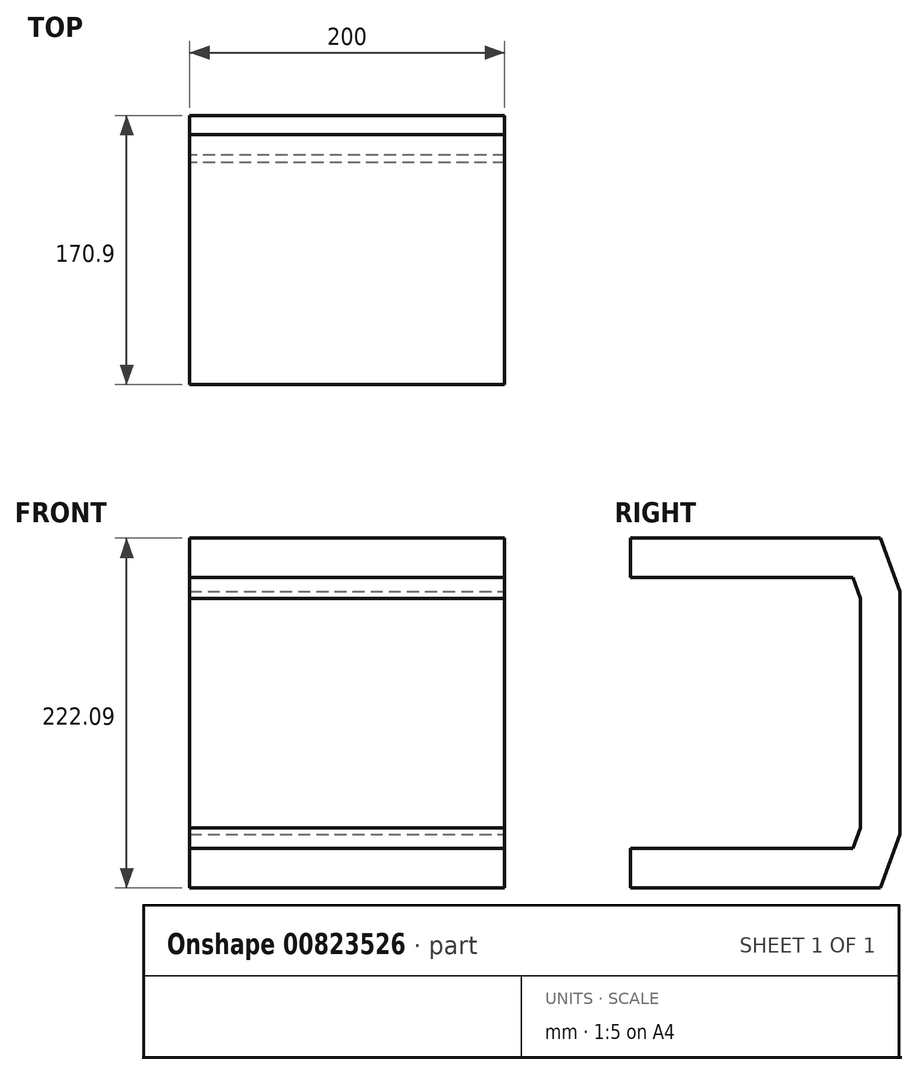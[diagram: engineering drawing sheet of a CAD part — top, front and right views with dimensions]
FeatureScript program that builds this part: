
annotation { "Feature Type Name" : "Feature", "Feature Type Description" : "" }
export const myFeature = defineFeature(function(context is Context, id is Id, definition is map)
    precondition{}
    {
        {
            var Q0;
            Q0=qCreatedBy(makeId("Front.planeOp"),FACE);
            var sketch = newSketch(context, id + "F0", { "sketchPlane" : qUnion([Q0])});
            skLineSegment(sketch, "E0.bottom", {"start": v(100, -12.5) * mm, "end": v(-100, -12.5) * mm});
            skLineSegment(sketch, "E0.top", {"start": v(100, 12.5) * mm, "end": v(-100, 12.5) * mm});
            skLineSegment(sketch, "E0.left", {"start": v(100, -12.5) * mm, "end": v(100, 12.5) * mm});
            skLineSegment(sketch, "E0.right", {"start": v(-100, -12.5) * mm, "end": v(-100, 12.5) * mm});
            skPoint(sketch, "E0.middle", {"position": v(0, 0) * mm});
            skSolve(sketch);
        }
        {
            var Q0;
            Q0=qCreatedBy(makeId("Right.planeOp"),FACE);
            var sketch = newSketch(context, id + "F1", { "sketchPlane" : qUnion([Q0])});
            skLineSegment(sketch, "E1", {"start": v(0, 0) * mm, "end": v(150, 0) * mm});
            skLineSegment(sketch, "E2", {"start": v(150, 0) * mm, "end": v(158.4, 23.55) * mm});
            skLineSegment(sketch, "E3", {"start": v(158.4, 23.55) * mm, "end": v(158.4, 173.55) * mm});
            skLineSegment(sketch, "E4", {"start": v(158.4, 173.55) * mm, "end": v(150, 197.1) * mm});
            skLineSegment(sketch, "E5", {"start": v(150, 197.1) * mm, "end": v(0, 197.1) * mm});
            skSolve(sketch);
        }
        {
            var Q0;
            Q0 = qSketchRegion(id + "F0", true);
            var Q1;
            Q1=sQuery(id+"F1.wireOp",EDGE,"E2");
            var Q2;
            Q2=sQuery(id+"F1.wireOp",EDGE,"E1");
            var Q3;
            Q3=sQuery(id+"F1.wireOp",EDGE,"E3");
            var Q4;
            Q4=sQuery(id+"F1.wireOp",EDGE,"E4");
            var Q5;
            Q5=sQuery(id+"F1.wireOp",EDGE,"E5");
            sweep(context, id + "F2", {"profiles" : qUnion([Q0]), "path" : qUnion([Q1, Q2, Q3, Q4, Q5])});
        }
    });
